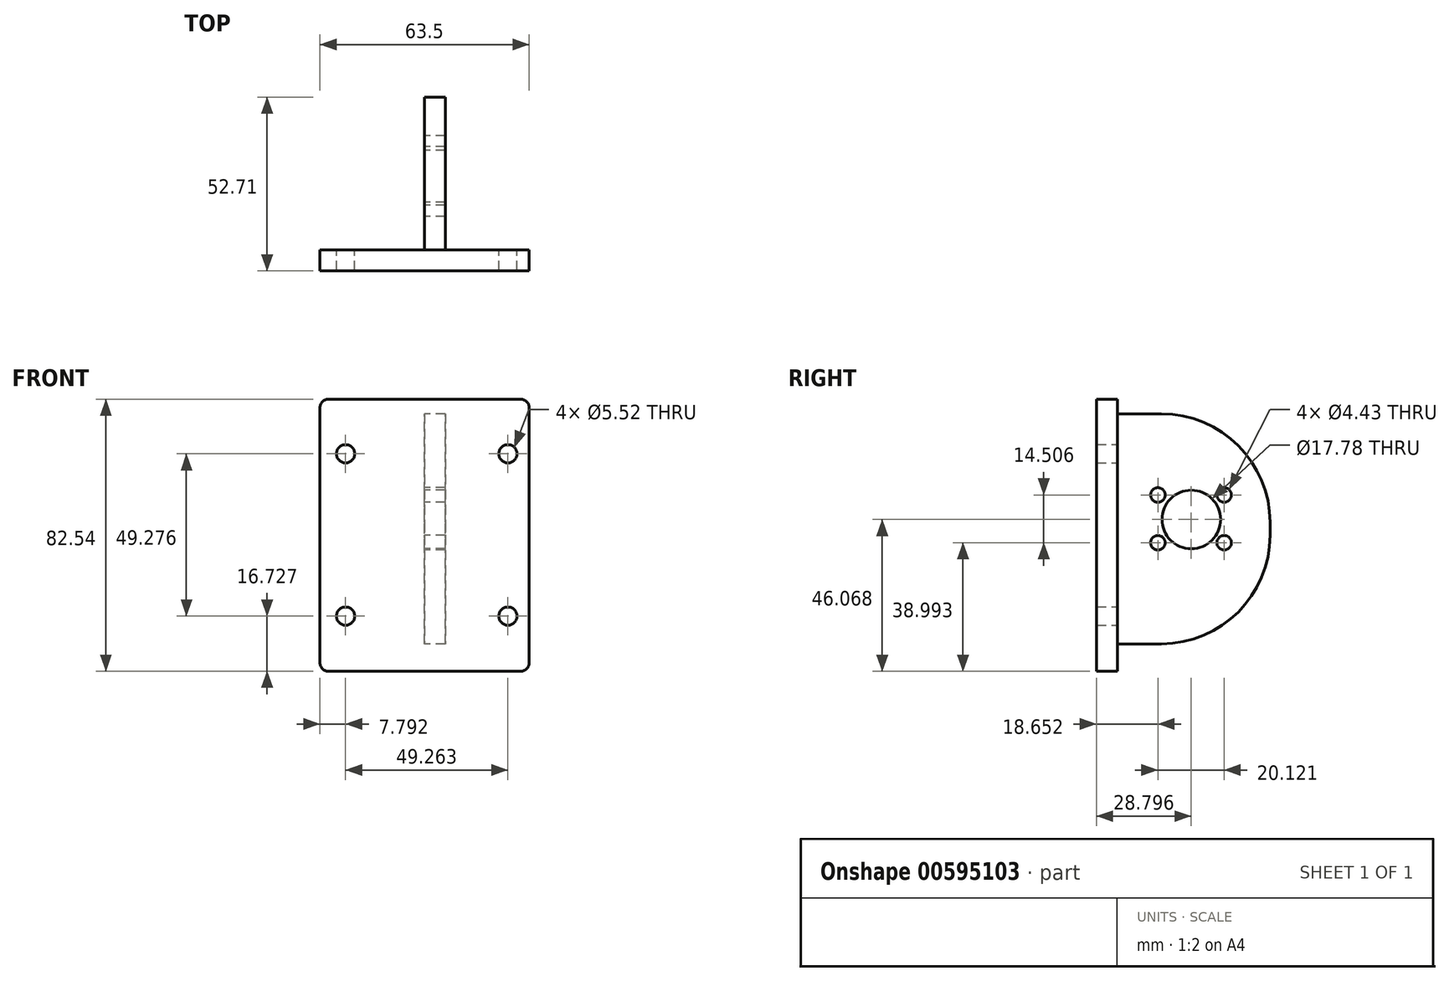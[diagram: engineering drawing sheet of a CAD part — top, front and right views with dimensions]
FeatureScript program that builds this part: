
annotation { "Feature Type Name" : "Feature", "Feature Type Description" : "" }
export const myFeature = defineFeature(function(context is Context, id is Id, definition is map)
    precondition{}
    {
        {
            var Q0;
            Q0=qCreatedBy(makeId("Front.planeOp"),FACE);
            var sketch = newSketch(context, id + "F0", { "sketchPlane" : qUnion([Q0])});
            skLineSegment(sketch, "E0.bottom", {"start": v(29.2, 41.28) * mm, "end": v(-29.21, 41.27) * mm});
            skLineSegment(sketch, "E0.top", {"start": v(29.21, -41.27) * mm, "end": v(-29.2, -41.28) * mm});
            skLineSegment(sketch, "E0.left", {"start": v(31.75, 38.74) * mm, "end": v(31.75, -38.73) * mm});
            skLineSegment(sketch, "E0.right", {"start": v(-31.75, 38.73) * mm, "end": v(-31.75, -38.74) * mm});
            skPoint(sketch, "E0.middle", {"position": v(0, 0) * mm});
            skCircle(sketch, "E1", {"center": v(-23.96, 24.73) * mm, "radius": 2.76 * mm});
            skCircle(sketch, "E2", {"center": v(25.3, 24.73) * mm, "radius": 2.76 * mm});
            skCircle(sketch, "E3", {"center": v(-23.96, -24.54) * mm, "radius": 2.76 * mm});
            skCircle(sketch, "E4", {"center": v(25.3, -24.54) * mm, "radius": 2.76 * mm});
            skPoint(sketch, "E5.visualSharp", {"position": v(-31.75, 41.27) * mm});
            skArc(sketch, "E5.filletArc", {"start": v(-29.21, 41.27) * mm, "mid": v(-31, 40.53) * mm, "end": v(-31.75, 38.73) * mm});
            skPoint(sketch, "E6.visualSharp", {"position": v(31.75, 41.28) * mm});
            skArc(sketch, "E6.filletArc", {"start": v(31.75, 38.74) * mm, "mid": v(31, 40.53) * mm, "end": v(29.2, 41.28) * mm});
            skPoint(sketch, "E7.visualSharp", {"position": v(31.75, -41.27) * mm});
            skArc(sketch, "E7.filletArc", {"start": v(29.21, -41.27) * mm, "mid": v(31, -40.53) * mm, "end": v(31.75, -38.73) * mm});
            skPoint(sketch, "E8.visualSharp", {"position": v(-31.75, -41.28) * mm});
            skArc(sketch, "E8.filletArc", {"start": v(-31.75, -38.74) * mm, "mid": v(-31, -40.53) * mm, "end": v(-29.2, -41.28) * mm});
            skSolve(sketch);
        }
        {
            var Q0;
            Q0=qCreatedBy(makeId("Right.planeOp"),FACE);
            var sketch = newSketch(context, id + "F1", { "sketchPlane" : qUnion([Q0])});
            skLineSegment(sketch, "E9.left", {"start": v(0, 36.86) * mm, "end": v(0, -33) * mm});
            skPoint(sketch, "E10.middle", {"position": v(0, 0) * mm});
            skLineSegment(sketch, "E11", {"start": v(0, 36.86) * mm, "end": v(13.37, 36.86) * mm});
            skLineSegment(sketch, "E12", {"start": v(46.36, 3.87) * mm, "end": v(46.36, 0) * mm});
            skLineSegment(sketch, "E13", {"start": v(13.37, -33) * mm, "end": v(0, -33) * mm});
            skPoint(sketch, "E14.visualSharp", {"position": v(46.36, 36.86) * mm});
            skArc(sketch, "E14.filletArc", {"start": v(46.36, 3.87) * mm, "mid": v(36.7, 27.2) * mm, "end": v(13.37, 36.86) * mm});
            skPoint(sketch, "E15.visualSharp", {"position": v(46.36, -33) * mm});
            skArc(sketch, "E15.filletArc", {"start": v(13.37, -33) * mm, "mid": v(36.7, -23.33) * mm, "end": v(46.36, 0) * mm});
            skCircle(sketch, "E16", {"center": v(22.45, 4.8) * mm, "radius": 8.9 * mm});
            skCircle(sketch, "E17", {"center": v(12.3, 12.23) * mm, "radius": 2.21 * mm});
            skCircle(sketch, "E18", {"center": v(32.42, 12.23) * mm, "radius": 2.21 * mm});
            skCircle(sketch, "E19", {"center": v(12.3, -2.28) * mm, "radius": 2.21 * mm});
            skCircle(sketch, "E20", {"center": v(32.42, -2.28) * mm, "radius": 2.21 * mm});
            skSolve(sketch);
        }
        {
            var Q0;
            Q0=makeQuery(id+"F0.imprint","IMPRINT",FACE,{"disambiguationData":[TD([[makeQuery(id+"F0.imprint","IMPRINT",EDGE,{"derivedFrom":sQuery(id+"F0.wireOp",EDGE,"E0.bottom")}),1.0]])]});
            extrude(context, id + "F2", {"entities" : qUnion([Q0]), "depth" : 6.35 * mm, "offsetDistance" : 25.4 * mm});
        }
        {
            var Q0;
            {var subQ1=sQuery(id+"F1.wireOp",EDGE,"E11");Q0=makeQuery(id+"F1.imprint","IMPRINT",FACE,{"disambiguationData":[TD([[makeQuery(id+"F1.imprint","IMPRINT",EDGE,{"derivedFrom":subQ1}),-1.0]])]});}
            extrude(context, id + "F3", {"entities" : qUnion([Q0]), "operationType" : NewBodyOperationType.ADD, "depth" : 6.35 * mm, "offsetDistance" : 25.4 * mm});
        }
    });
